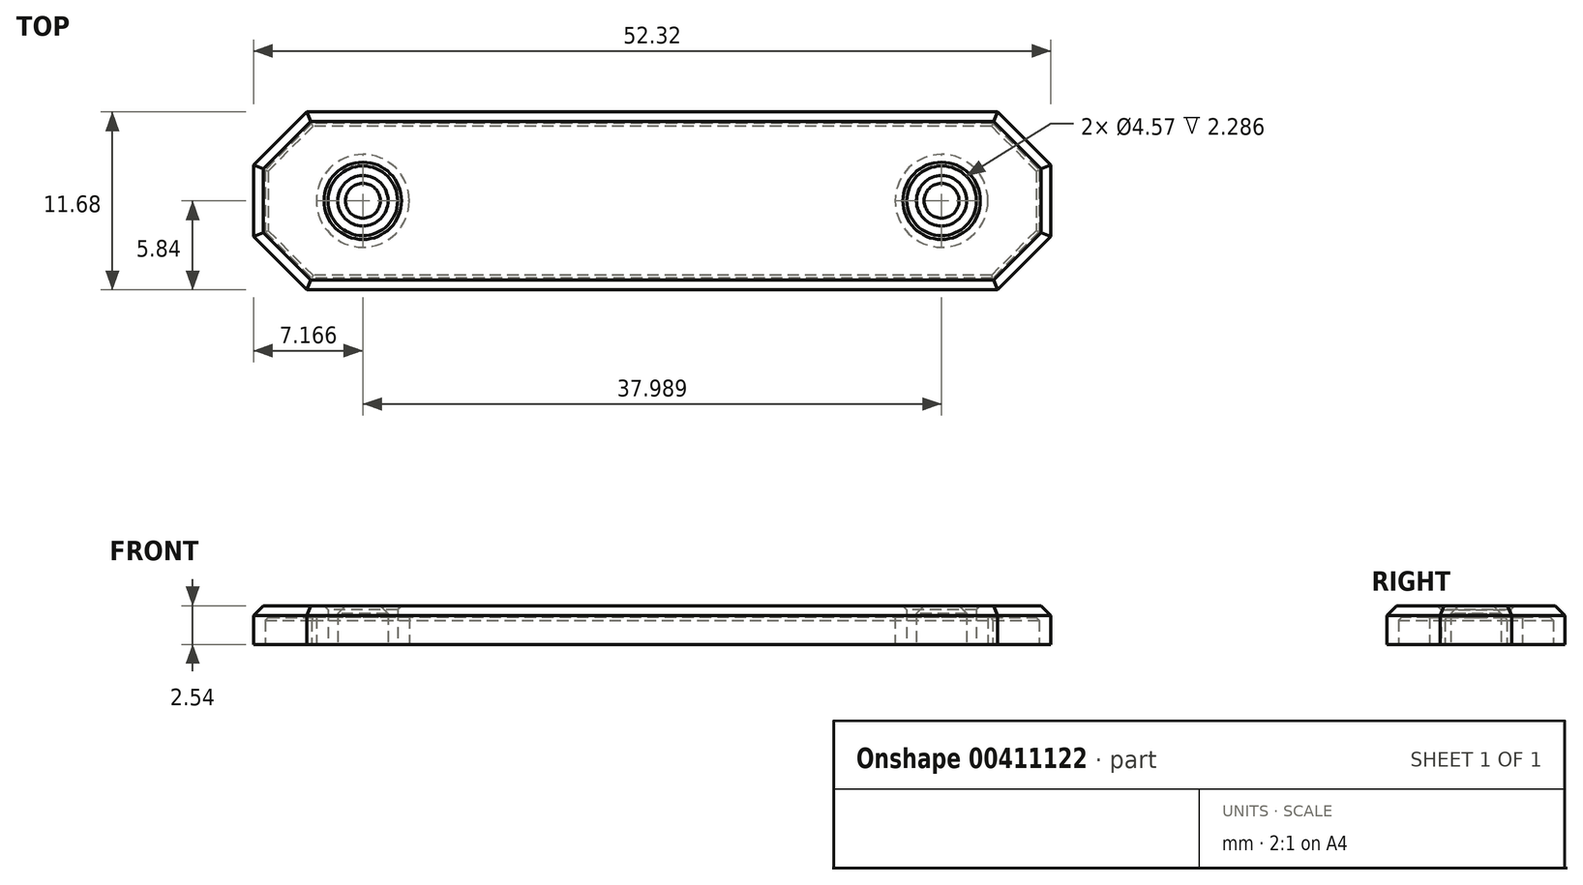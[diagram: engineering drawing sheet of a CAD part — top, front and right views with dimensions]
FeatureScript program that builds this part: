
annotation { "Feature Type Name" : "Feature", "Feature Type Description" : "" }
export const myFeature = defineFeature(function(context is Context, id is Id, definition is map)
    precondition{}
    {
        {
            var Q0;
            Q0=qCreatedBy(makeId("Top.planeOp"),FACE);
            var sketch = newSketch(context, id + "F0", { "sketchPlane" : qUnion([Q0])});
            skLineSegment(sketch, "E0.bottom", {"start": v(-44.45, 25.4) * mm, "end": v(44.45, 25.4) * mm});
            skLineSegment(sketch, "E0.top", {"start": v(-44.45, -25.4) * mm, "end": v(44.45, -25.4) * mm});
            skLineSegment(sketch, "E0.left", {"start": v(-44.45, 25.4) * mm, "end": v(-44.45, -25.4) * mm});
            skLineSegment(sketch, "E0.right", {"start": v(44.45, 25.4) * mm, "end": v(44.45, -25.4) * mm});
            skPoint(sketch, "E0.middle", {"position": v(0, 0) * mm});
            skLineSegment(sketch, "E1.bottom", {"start": v(-44.45, 25.4) * mm, "end": v(-19, 25.4) * mm});
            skLineSegment(sketch, "E1.top", {"start": v(-44.45, -25.4) * mm, "end": v(-19, -25.4) * mm});
            skLineSegment(sketch, "E1.right", {"start": v(-19, 25.4) * mm, "end": v(-19, -25.4) * mm});
            skLineSegment(sketch, "E2.MirrorCS", {"start": v(19, 25.4) * mm, "end": v(19, -25.4) * mm});
            skCircle(sketch, "E3", {"center": v(-19, 0) * mm, "radius": 2.29 * mm});
            skCircle(sketch, "E4.0", {"center": v(-19, 0) * mm, "radius": 1.65 * mm});
            skLineSegment(sketch, "E5.0", {"start": v(-46.99, 27.94) * mm, "end": v(-19, 27.94) * mm});
            skLineSegment(sketch, "E5.1", {"start": v(-46.99, 27.94) * mm, "end": v(-46.99, -27.94) * mm});
            skLineSegment(sketch, "E5.2", {"start": v(-46.99, -27.94) * mm, "end": v(-19, -27.94) * mm});
            skLineSegment(sketch, "E6", {"start": v(-19, 27.94) * mm, "end": v(-19, 25.4) * mm});
            skLineSegment(sketch, "E7", {"start": v(-19, -25.4) * mm, "end": v(-19, -27.94) * mm});
            skLineSegment(sketch, "E8.MirrorCS", {"start": v(19, 27.94) * mm, "end": v(19, 25.4) * mm});
            skLineSegment(sketch, "E9.MirrorCS", {"start": v(46.99, 27.94) * mm, "end": v(19, 27.94) * mm});
            skLineSegment(sketch, "E10.MirrorCS", {"start": v(46.99, 27.94) * mm, "end": v(46.99, -27.94) * mm});
            skLineSegment(sketch, "E11.MirrorCS", {"start": v(46.99, -27.94) * mm, "end": v(19, -27.94) * mm});
            skLineSegment(sketch, "E12.MirrorCS", {"start": v(19, -25.4) * mm, "end": v(19, -27.94) * mm});
            skLineSegment(sketch, "E13.bottom", {"start": v(22.35, 5.08) * mm, "end": v(-22.35, 5.08) * mm});
            skLineSegment(sketch, "E13.top", {"start": v(22.35, -5.08) * mm, "end": v(-22.35, -5.08) * mm});
            skLineSegment(sketch, "E13.left", {"start": v(25.4, 2.03) * mm, "end": v(25.4, -2.03) * mm});
            skLineSegment(sketch, "E13.right", {"start": v(-25.4, 2.03) * mm, "end": v(-25.4, -2.03) * mm});
            skLineSegment(sketch, "E14", {"start": v(-22.35, 5.08) * mm, "end": v(-25.4, 2.03) * mm});
            skLineSegment(sketch, "E15", {"start": v(-25.4, -2.03) * mm, "end": v(-22.35, -5.08) * mm});
            skLineSegment(sketch, "E16", {"start": v(22.35, 5.08) * mm, "end": v(25.4, 2.03) * mm});
            skLineSegment(sketch, "E17", {"start": v(25.4, -2.03) * mm, "end": v(22.35, -5.08) * mm});
            skLineSegment(sketch, "E18.0", {"start": v(22.67, 5.84) * mm, "end": v(26.16, 2.35) * mm});
            skLineSegment(sketch, "E18.1", {"start": v(26.16, 2.35) * mm, "end": v(26.16, -2.35) * mm});
            skLineSegment(sketch, "E18.2", {"start": v(22.67, 5.84) * mm, "end": v(-22.67, 5.84) * mm});
            skLineSegment(sketch, "E18.3", {"start": v(26.16, -2.35) * mm, "end": v(22.67, -5.84) * mm});
            skLineSegment(sketch, "E18.4", {"start": v(-22.67, 5.84) * mm, "end": v(-26.16, 2.35) * mm});
            skLineSegment(sketch, "E18.5", {"start": v(-26.16, 2.35) * mm, "end": v(-26.16, -2.35) * mm});
            skLineSegment(sketch, "E18.6", {"start": v(-26.16, -2.35) * mm, "end": v(-22.67, -5.84) * mm});
            skLineSegment(sketch, "E18.7", {"start": v(22.67, -5.84) * mm, "end": v(-22.67, -5.84) * mm});
            skCircle(sketch, "E19.MirrorC", {"center": v(19, 0) * mm, "radius": 2.29 * mm});
            skCircle(sketch, "E20.MirrorC", {"center": v(19, 0) * mm, "radius": 1.65 * mm});
            skSolve(sketch);
        }
        {
            var Q0;
            {var subQ0=sQuery(id+"F0.wireOp",EDGE,"E3");var subQ1=sQuery(id+"F0.wireOp",EDGE,"E1.right");var subQ2=makeQuery(id+"F0.imprint","INTERSECT",VERTEX,{"disambiguationData":[OD(0.0)],"derivedFrom":[subQ1,subQ0]});Q0=makeQuery(id+"F0.imprint","IMPRINT",FACE,{"disambiguationData":[TD([[makeQuery(id+"F0.imprint","IMPRINT",EDGE,{"disambiguationData":[TD([[subQ2,-1.0]])],"derivedFrom":subQ1}),-1.0]])]});}
            var Q1;
            {var subQ0=sQuery(id+"F0.wireOp",EDGE,"E3");var subQ1=sQuery(id+"F0.wireOp",EDGE,"E1.right");var subQ2=makeQuery(id+"F0.imprint","INTERSECT",VERTEX,{"disambiguationData":[OD(0.0)],"derivedFrom":[subQ1,subQ0]});Q1=makeQuery(id+"F0.imprint","IMPRINT",FACE,{"disambiguationData":[TD([[makeQuery(id+"F0.imprint","IMPRINT",EDGE,{"disambiguationData":[TD([[subQ2,-1.0]])],"derivedFrom":subQ1}),1.0]])]});}
            var Q2;
            {var subQ0=sQuery(id+"F0.wireOp",EDGE,"E19.MirrorC");var subQ1=sQuery(id+"F0.wireOp",EDGE,"E2.MirrorCS");var subQ2=makeQuery(id+"F0.imprint","INTERSECT",VERTEX,{"disambiguationData":[OD(0.0)],"derivedFrom":[subQ1,subQ0]});Q2=makeQuery(id+"F0.imprint","IMPRINT",FACE,{"disambiguationData":[TD([[makeQuery(id+"F0.imprint","IMPRINT",EDGE,{"disambiguationData":[TD([[subQ2,-1.0]])],"derivedFrom":subQ1}),1.0]])]});}
            var Q3;
            {var subQ0=sQuery(id+"F0.wireOp",EDGE,"E19.MirrorC");var subQ1=sQuery(id+"F0.wireOp",EDGE,"E2.MirrorCS");var subQ2=makeQuery(id+"F0.imprint","INTERSECT",VERTEX,{"disambiguationData":[OD(0.0)],"derivedFrom":[subQ1,subQ0]});Q3=makeQuery(id+"F0.imprint","IMPRINT",FACE,{"disambiguationData":[TD([[makeQuery(id+"F0.imprint","IMPRINT",EDGE,{"disambiguationData":[TD([[subQ2,-1.0]])],"derivedFrom":subQ1}),-1.0]])]});}
            extrude(context, id + "F1", {"entities" : qUnion([Q0, Q1, Q2, Q3]), "depth" : 2.03 * mm});
        }
        {
            var Q0;
            Q0=makeQuery(id+"F0.imprint","IMPRINT",FACE,{"disambiguationData":[TD([[makeQuery(id+"F0.imprint","IMPRINT",EDGE,{"derivedFrom":sQuery(id+"F0.wireOp",EDGE,"E13.right")}),1.0]])]});
            var Q1;
            {var subQ5=sQuery(id+"F0.wireOp",EDGE,"E13.bottom");var subQ8=sQuery(id+"F0.wireOp",EDGE,"E1.right");var subQ9=makeQuery(id+"F0.imprint","INTERSECT",VERTEX,{"derivedFrom":[subQ8,subQ5]});Q1=makeQuery(id+"F0.imprint","IMPRINT",FACE,{"disambiguationData":[TD([[makeQuery(id+"F0.imprint","IMPRINT",EDGE,{"disambiguationData":[TD([[subQ9,-1.0]])],"derivedFrom":subQ8}),1.0]])]});}
            var Q2;
            {var subQ0=sQuery(id+"F0.wireOp",EDGE,"E4.0");var subQ1=sQuery(id+"F0.wireOp",EDGE,"E1.right");var subQ2=makeQuery(id+"F0.imprint","INTERSECT",VERTEX,{"disambiguationData":[OD(0.0)],"derivedFrom":[subQ1,subQ0]});Q2=makeQuery(id+"F0.imprint","IMPRINT",FACE,{"disambiguationData":[TD([[makeQuery(id+"F0.imprint","IMPRINT",EDGE,{"disambiguationData":[TD([[subQ2,-1.0]])],"derivedFrom":subQ1}),1.0]])]});}
            var Q3;
            {var subQ0=sQuery(id+"F0.wireOp",EDGE,"E4.0");var subQ1=sQuery(id+"F0.wireOp",EDGE,"E1.right");var subQ2=makeQuery(id+"F0.imprint","INTERSECT",VERTEX,{"disambiguationData":[OD(0.0)],"derivedFrom":[subQ1,subQ0]});Q3=makeQuery(id+"F0.imprint","IMPRINT",FACE,{"disambiguationData":[TD([[makeQuery(id+"F0.imprint","IMPRINT",EDGE,{"disambiguationData":[TD([[subQ2,-1.0]])],"derivedFrom":subQ1}),-1.0]])]});}
            var Q4;
            {var subQ0=sQuery(id+"F0.wireOp",EDGE,"E20.MirrorC");var subQ1=sQuery(id+"F0.wireOp",EDGE,"E2.MirrorCS");var subQ2=makeQuery(id+"F0.imprint","INTERSECT",VERTEX,{"disambiguationData":[OD(0.0)],"derivedFrom":[subQ1,subQ0]});Q4=makeQuery(id+"F0.imprint","IMPRINT",FACE,{"disambiguationData":[TD([[makeQuery(id+"F0.imprint","IMPRINT",EDGE,{"disambiguationData":[TD([[subQ2,-1.0]])],"derivedFrom":subQ1}),1.0]])]});}
            var Q5;
            {var subQ0=sQuery(id+"F0.wireOp",EDGE,"E20.MirrorC");var subQ1=sQuery(id+"F0.wireOp",EDGE,"E2.MirrorCS");var subQ2=makeQuery(id+"F0.imprint","INTERSECT",VERTEX,{"disambiguationData":[OD(0.0)],"derivedFrom":[subQ1,subQ0]});Q5=makeQuery(id+"F0.imprint","IMPRINT",FACE,{"disambiguationData":[TD([[makeQuery(id+"F0.imprint","IMPRINT",EDGE,{"disambiguationData":[TD([[subQ2,-1.0]])],"derivedFrom":subQ1}),-1.0]])]});}
            var Q6;
            Q6=makeQuery(id+"F0.imprint","IMPRINT",FACE,{"disambiguationData":[TD([[makeQuery(id+"F0.imprint","IMPRINT",EDGE,{"derivedFrom":sQuery(id+"F0.wireOp",EDGE,"E13.left")}),-1.0]])]});
            var Q7;
            {var subQ0=sQuery(id+"F0.wireOp",EDGE,"E18.2");var subQ1=sQuery(id+"F0.wireOp",EDGE,"E1.right");var subQ2=makeQuery(id+"F0.imprint","INTERSECT",VERTEX,{"derivedFrom":[subQ1,subQ0]});Q7=makeQuery(id+"F0.imprint","IMPRINT",FACE,{"disambiguationData":[TD([[makeQuery(id+"F0.imprint","IMPRINT",EDGE,{"disambiguationData":[TD([[subQ2,-1.0]])],"derivedFrom":subQ1}),1.0]])]});}
            var Q8;
            Q8=makeQuery(id+"F0.imprint","IMPRINT",FACE,{"disambiguationData":[TD([[makeQuery(id+"F0.imprint","IMPRINT",EDGE,{"derivedFrom":sQuery(id+"F0.wireOp",EDGE,"E13.right")}),-1.0]])]});
            var Q9;
            {var subQ0=sQuery(id+"F0.wireOp",EDGE,"E13.top");var subQ1=sQuery(id+"F0.wireOp",EDGE,"E1.right");var subQ2=makeQuery(id+"F0.imprint","INTERSECT",VERTEX,{"derivedFrom":[subQ1,subQ0]});Q9=makeQuery(id+"F0.imprint","IMPRINT",FACE,{"disambiguationData":[TD([[makeQuery(id+"F0.imprint","IMPRINT",EDGE,{"disambiguationData":[TD([[subQ2,-1.0]])],"derivedFrom":subQ1}),1.0]])]});}
            var Q10;
            Q10=makeQuery(id+"F0.imprint","IMPRINT",FACE,{"disambiguationData":[TD([[makeQuery(id+"F0.imprint","IMPRINT",EDGE,{"derivedFrom":sQuery(id+"F0.wireOp",EDGE,"E13.left")}),1.0]])]});
            extrude(context, id + "F2", {"entities" : qUnion([Q0, Q1, Q2, Q3, Q4, Q5, Q6, Q7, Q8, Q9, Q10]), "depth" : 2.54 * mm});
        }
        {
            var Q0;
            Q0=makeQuery(id+"F2.opExtrude","CAP_FACE",FACE,{"disambiguationData":[OSD([sQuery(id+"F0.wireOp",EDGE,"E4.0")])],"isStart":false});
            var Q1;
            Q1=makeQuery(id+"F2.opExtrude","CAP_FACE",FACE,{"disambiguationData":[OSD([sQuery(id+"F0.wireOp",EDGE,"E20.MirrorC")])],"isStart":false});
            chamfer(context, id + "F3", {"entities" : qUnion([Q0, Q1]), "width" : 0.5 * mm, "tangentPropagation" : true});
        }
        {
            var Q0;
            Q0=makeQuery(id+"F2.opExtrude","CAP_EDGE",EDGE,{"disambiguationData":[OSD([sQuery(id+"F0.wireOp",EDGE,"E18.2")])],"isStart":false});
            var Q1;
            Q1=makeQuery(id+"F2.opExtrude","CAP_EDGE",EDGE,{"disambiguationData":[OSD([sQuery(id+"F0.wireOp",EDGE,"E18.4")])],"isStart":false});
            var Q2;
            Q2=makeQuery(id+"F2.opExtrude","CAP_EDGE",EDGE,{"disambiguationData":[OSD([sQuery(id+"F0.wireOp",EDGE,"E18.5")])],"isStart":false});
            var Q3;
            Q3=makeQuery(id+"F2.opExtrude","CAP_EDGE",EDGE,{"disambiguationData":[OSD([sQuery(id+"F0.wireOp",EDGE,"E18.6")])],"isStart":false});
            var Q4;
            Q4=makeQuery(id+"F2.opExtrude","CAP_EDGE",EDGE,{"disambiguationData":[OSD([sQuery(id+"F0.wireOp",EDGE,"E18.7")])],"isStart":false});
            var Q5;
            Q5=makeQuery(id+"F2.opExtrude","CAP_EDGE",EDGE,{"disambiguationData":[OSD([sQuery(id+"F0.wireOp",EDGE,"E18.1")])],"isStart":false});
            var Q6;
            Q6=makeQuery(id+"F2.opExtrude","CAP_EDGE",EDGE,{"disambiguationData":[OSD([sQuery(id+"F0.wireOp",EDGE,"E18.0")])],"isStart":false});
            var Q7;
            Q7=makeQuery(id+"F2.opExtrude","CAP_EDGE",EDGE,{"disambiguationData":[OSD([sQuery(id+"F0.wireOp",EDGE,"E18.3")])],"isStart":false});
            chamfer(context, id + "F4", {"entities" : qUnion([Q0, Q1, Q2, Q3, Q4, Q5, Q6, Q7]), "width" : 0.64 * mm, "tangentPropagation" : true});
        }
        {
            var Q0;
            Q0=makeQuery(id+"F2.opExtrude","CAP_EDGE",EDGE,{"disambiguationData":[OSD([sQuery(id+"F0.wireOp",EDGE,"E3")])],"isStart":false});
            var Q1;
            Q1=makeQuery(id+"F2.opExtrude","CAP_EDGE",EDGE,{"disambiguationData":[OSD([sQuery(id+"F0.wireOp",EDGE,"E19.MirrorC")])],"isStart":false});
            chamfer(context, id + "F5", {"entities" : qUnion([Q0, Q1]), "width" : 0.25 * mm, "tangentPropagation" : true});
        }
        {
            var Q0;
            Q0=makeQuery(id+"F2.opExtrude","SWEPT_BODY",BODY,{"disambiguationData":[OSD([sQuery(id+"F0.wireOp",EDGE,"E20.MirrorC")])]});
            var Q1;
            Q1=makeQuery(id+"F1.opExtrude","SWEPT_BODY",BODY,{"disambiguationData":[OSD([sQuery(id+"F0.wireOp",EDGE,"E3"),sQuery(id+"F0.wireOp",EDGE,"E4.0")])]});
            var Q2;
            Q2=makeQuery(id+"F1.opExtrude","SWEPT_BODY",BODY,{"disambiguationData":[OSD([sQuery(id+"F0.wireOp",EDGE,"E19.MirrorC"),sQuery(id+"F0.wireOp",EDGE,"E20.MirrorC")])]});
            var Q3;
            Q3=makeQuery(id+"F2.opExtrude","SWEPT_BODY",BODY,{"disambiguationData":[OSD([sQuery(id+"F0.wireOp",EDGE,"E4.0")])]});
            var Q4;
            Q4=makeQuery(id+"F2.opExtrude","SWEPT_BODY",BODY,{"disambiguationData":[OSD([sQuery(id+"F0.wireOp",EDGE,"E3"),sQuery(id+"F0.wireOp",EDGE,"E18.0"),sQuery(id+"F0.wireOp",EDGE,"E18.1"),sQuery(id+"F0.wireOp",EDGE,"E18.2"),sQuery(id+"F0.wireOp",EDGE,"E18.3"),sQuery(id+"F0.wireOp",EDGE,"E18.4"),sQuery(id+"F0.wireOp",EDGE,"E18.5"),sQuery(id+"F0.wireOp",EDGE,"E18.6"),sQuery(id+"F0.wireOp",EDGE,"E18.7"),sQuery(id+"F0.wireOp",EDGE,"E19.MirrorC")])]});
            booleanBodies(context, id + "F6", {"operationType" : BooleanOperationType.UNION, "tools" : qUnion([Q0, Q1, Q2, Q3, Q4])});
        }
        {
            var Q0;
            {var subQ0=sQuery(id+"F0.wireOp",EDGE,"E20.MirrorC");var subQ1=sQuery(id+"F0.wireOp",EDGE,"E4.0");var subQ2=sQuery(id+"F0.wireOp",EDGE,"E19.MirrorC");var subQ3=sQuery(id+"F0.wireOp",EDGE,"E3");Q0=makeQuery(id+"F6.opBoolean","MERGE",FACE,{"derivedFrom":[makeQuery(id+"F1.opExtrude","CAP_FACE",FACE,{"disambiguationData":[OSD([subQ3,subQ1])],"isStart":true}),makeQuery(id+"F1.opExtrude","CAP_FACE",FACE,{"disambiguationData":[OSD([subQ2,subQ0])],"isStart":true}),makeQuery(id+"F2.opExtrude","CAP_FACE",FACE,{"disambiguationData":[OSD([subQ3,sQuery(id+"F0.wireOp",EDGE,"E18.0"),sQuery(id+"F0.wireOp",EDGE,"E18.1"),sQuery(id+"F0.wireOp",EDGE,"E18.2"),sQuery(id+"F0.wireOp",EDGE,"E18.3"),sQuery(id+"F0.wireOp",EDGE,"E18.4"),sQuery(id+"F0.wireOp",EDGE,"E18.5"),sQuery(id+"F0.wireOp",EDGE,"E18.6"),sQuery(id+"F0.wireOp",EDGE,"E18.7"),subQ2])],"isStart":true}),makeQuery(id+"F2.opExtrude","CAP_FACE",FACE,{"disambiguationData":[OSD([subQ1])],"isStart":true}),makeQuery(id+"F2.opExtrude","CAP_FACE",FACE,{"disambiguationData":[OSD([subQ0])],"isStart":true})]});}
            shell(context, id + "F7", {"entities" : qUnion([Q0]), "thickness" : 0.76 * mm});
        }
    });
